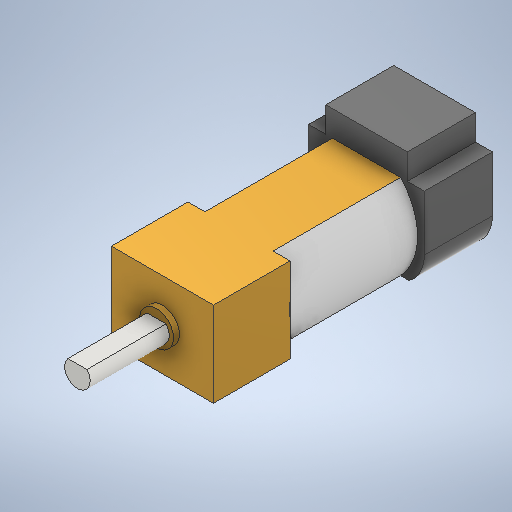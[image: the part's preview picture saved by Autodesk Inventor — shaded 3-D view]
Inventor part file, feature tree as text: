
AUTODESK INVENTOR PART (.ipt)
format: ipt  version: 2025 (Build 290162000, 162)  size: 289,792 bytes
history: native  units: mm
features: extrude x5, sketch x4, other x1
ambient origin geometry x8: Origin, YZ Plane, XZ Plane, XY Plane, X Axis, Y Axis, Z Axis, Center Point
bodies: Body1 (feature_tree)
feature tree (10):
  other  "ソリッド1"
  extrude  "ギヤボックス"  Depth=12.0mm
  sketch  "スケッチ2"
  extrude  "軸受け"  Depth=10.0mm
  extrude  "軸"  Depth=9.0mm TaperAngle=0.0deg
  extrude  "モーター"  Depth=3.0mm
  extrude  "エンコーダ"  Depth=1.0mm
  sketch  "スケッチ1"
  sketch  "スケッチ3"
  sketch  "スケッチ4"
